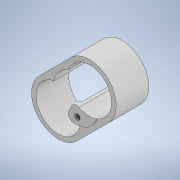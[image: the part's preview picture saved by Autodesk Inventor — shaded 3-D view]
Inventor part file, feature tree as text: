
AUTODESK INVENTOR PART (.ipt)
format: ipt  version: 2020 (Build 240168000, 168)  size: 171,520 bytes
history: native  units: in
note: dims shown in document units (in); Inventor stores cm internally (conversion verified against a paired STEP export)
features: sketch x5, other x3, extrude x1
ambient origin geometry x8: Origin, YZ Plane, XZ Plane, XY Plane, X Axis, Y Axis, Z Axis, Center Point
bodies: Solid1 (feature_tree)
feature tree (9):
  other  "Hiolder_25.ipt"
  extrude  "Extrusion1"  Depth=0.0098in TaperAngle=0.0deg
  other  "Solid1::Hiolder_25.ipt"
  other  "TaggingFeature1"
  sketch  "Sketch1"  dims[d0=0.3937in d1=0.0098in d2=0.0in]
  sketch  "Sketch3"
  sketch  "Sketch4"
  sketch  "Sketch5"
  sketch  "Sketch6"
